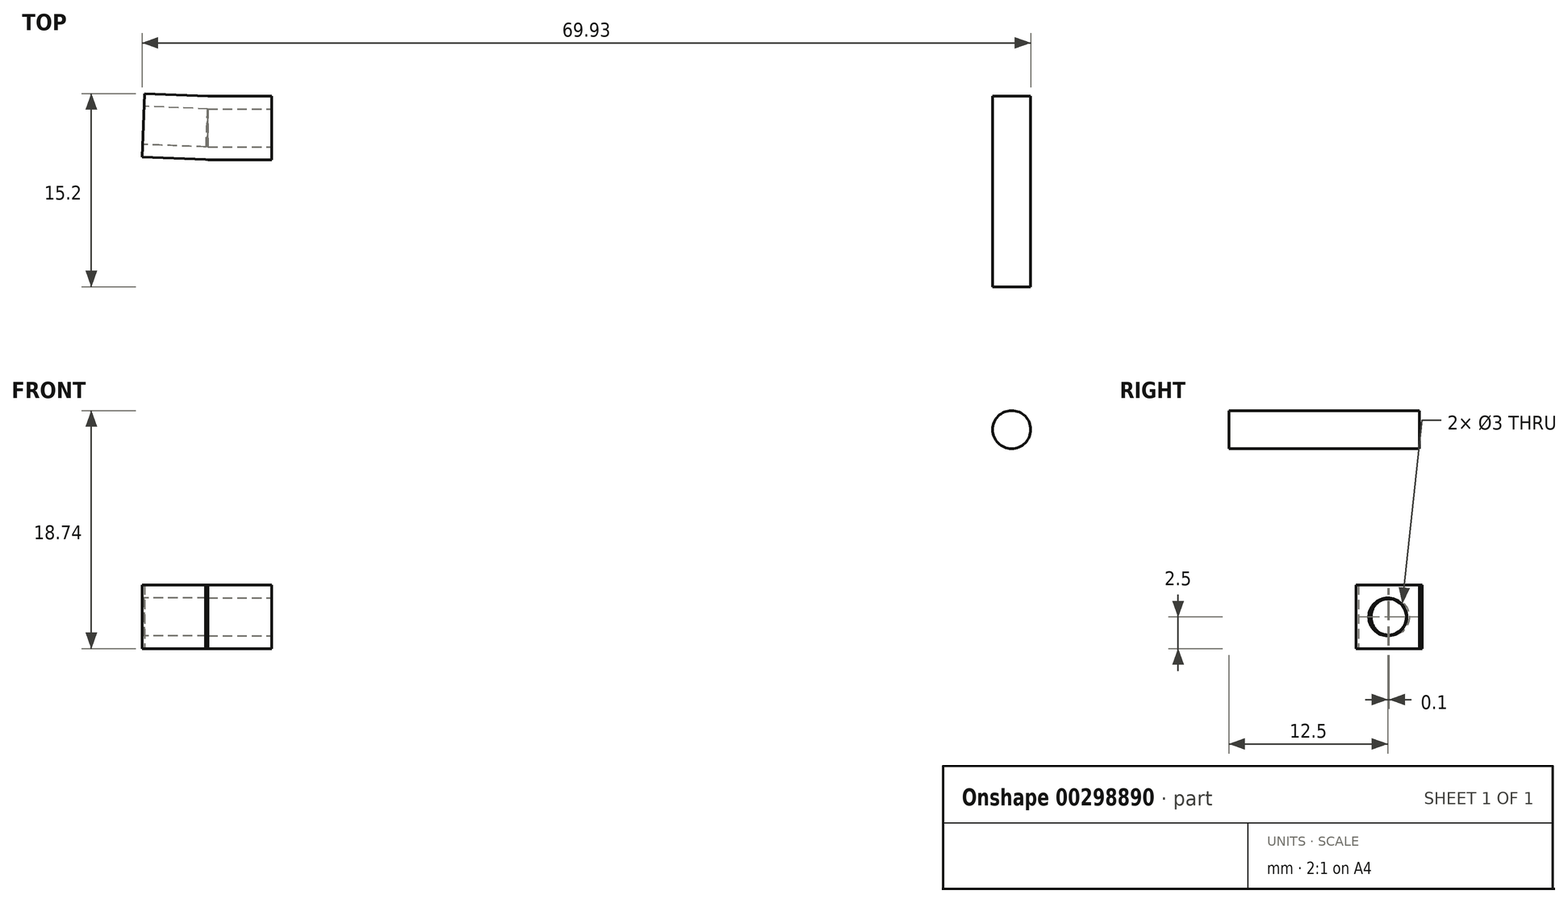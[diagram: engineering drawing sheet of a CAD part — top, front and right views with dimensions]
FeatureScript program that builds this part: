
annotation { "Feature Type Name" : "Feature", "Feature Type Description" : "" }
export const myFeature = defineFeature(function(context is Context, id is Id, definition is map)
    precondition{}
    {
        {
            var Q0;
            Q0=qCreatedBy(makeId("Top.planeOp"),FACE);
            var sketch = newSketch(context, id + "F0", { "sketchPlane" : qUnion([Q0])});
            skLineSegment(sketch, "E0", {"start": v(0, 0) * mm, "end": v(-5, 0) * mm});
            skLineSegment(sketch, "E1", {"start": v(-5, 0) * mm, "end": v(-10, 0.2) * mm});
            skLineSegment(sketch, "E2", {"start": v(-5, 0) * mm, "end": v(-5, -5) * mm});
            skLineSegment(sketch, "E3", {"start": v(-5, -5) * mm, "end": v(0, -5) * mm});
            skLineSegment(sketch, "E4", {"start": v(0, -5) * mm, "end": v(0, 0) * mm});
            skLineSegment(sketch, "E5", {"start": v(-10, 0.2) * mm, "end": v(-10.2, -4.8) * mm});
            skLineSegment(sketch, "E6", {"start": v(-10.2, -4.8) * mm, "end": v(-5.2, -5) * mm});
            skLineSegment(sketch, "E7", {"start": v(-5.2, -5) * mm, "end": v(-5, 0) * mm});
            skLineSegment(sketch, "E8", {"start": v(-5.2, -5) * mm, "end": v(-5, -5) * mm});
            skSolve(sketch);
        }
        {
            var Q0;
            Q0 = qSketchRegion(id + "F0", true);
            extrude(context, id + "F1", {"entities" : qUnion([Q0]), "depth" : 5 * mm});
        }
        {
            var Q0;
            Q0=makeQuery(id+"F1.opExtrude","SWEPT_FACE",FACE,{"disambiguationData":[OSD([sQuery(id+"F0.wireOp",EDGE,"E5")])]});
            var sketch = newSketch(context, id + "F2", { "sketchPlane" : qUnion([Q0])});
            skCircle(sketch, "E9", {"center": v(2.7, 2.5) * mm, "radius": 1.5 * mm});
            skPoint(sketch, "E9.centerSnap0", {"position": v(0.2, 2.5) * mm});
            skPoint(sketch, "E9.centerSnap1", {"position": v(2.7, 0) * mm});
            skSolve(sketch);
        }
        {
            var Q0;
            Q0=makeQuery(id+"F1.opExtrude","SWEPT_FACE",FACE,{"disambiguationData":[OSD([sQuery(id+"F0.wireOp",EDGE,"E4")])]});
            var sketch = newSketch(context, id + "F3", { "sketchPlane" : qUnion([Q0])});
            skCircle(sketch, "E10", {"center": v(-2.5, 2.5) * mm, "radius": 1.5 * mm});
            skPoint(sketch, "E10.centerSnap0", {"position": v(-2.5, 5) * mm});
            skPoint(sketch, "E10.centerSnap1", {"position": v(0, 2.5) * mm});
            skSolve(sketch);
        }
        {
            var Q0;
            Q0=sQuery(id+"F3.wireOp",VERTEX,"E10.center");
            var Q1;
            Q1=sQuery(id+"F2.wireOp",VERTEX,"E9.center");
            var Q2;
            Q2=makeQuery(id+"F1.opExtrude","SWEPT_BODY",BODY,{"disambiguationData":[OSD([sQuery(id+"F0.wireOp",EDGE,"E0"),sQuery(id+"F0.wireOp",EDGE,"E1"),sQuery(id+"F0.wireOp",EDGE,"E3"),sQuery(id+"F0.wireOp",EDGE,"E4"),sQuery(id+"F0.wireOp",EDGE,"E5"),sQuery(id+"F0.wireOp",EDGE,"E6"),sQuery(id+"F0.wireOp",EDGE,"E8")])]});
            hole(context, id + "F4", {"style" : HoleStyle.SIMPLE, "endStyle" : HoleEndStyle.BLIND, "holeDiameter" : 3 * mm, "holeDepth" : 5 * mm, "tappedDepth" : 12 * mm, "tapClearance" : 3, "startFromSketch" : true, "locations" : qUnion([Q0, Q1]), "scope" : qUnion([Q2])});
        }
        {
            var Q0;
            Q0=qCreatedBy(makeId("Front.planeOp"),FACE);
            var sketch = newSketch(context, id + "F5", { "sketchPlane" : qUnion([Q0])});
            skCircle(sketch, "E11", {"center": v(58.24, 17.24) * mm, "radius": 1.5 * mm});
            skSolve(sketch);
        }
        {
            var Q0;
            Q0 = qSketchRegion(id + "F5", true);
            extrude(context, id + "F6", {"entities" : qUnion([Q0]), "depth" : 15 * mm});
        }
    });
